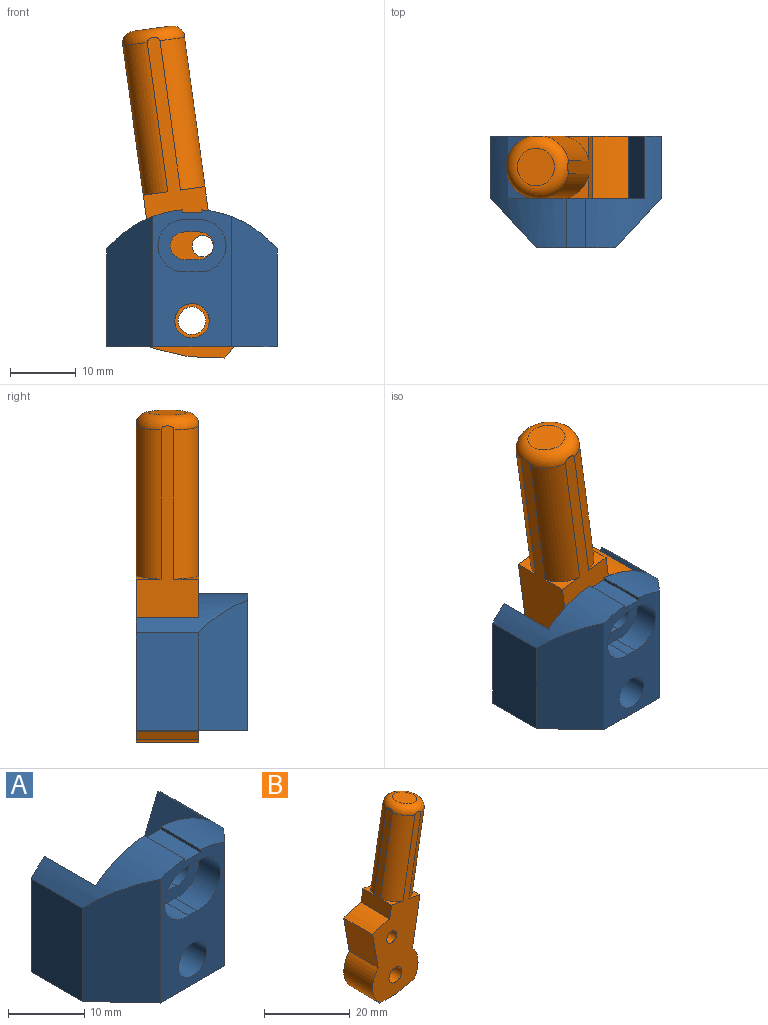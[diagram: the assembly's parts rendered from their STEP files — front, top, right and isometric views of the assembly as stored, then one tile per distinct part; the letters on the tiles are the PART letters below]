
ASSEMBLY  parts=2 mates=1
PART A: 28 faces, bbox 26x17x20.9 mm
  f0: plane 26x17mm, normal (0,0,-1), area 269mm2, adj f2,f8,f9,f10,f11,f12,f15,f16
  f1: cylinder r=17mm len=17mm, axis (0,1,0), area 98.1mm2, adj f2,f8,f11,f14,f16,f25,f27
  f2: plane 20.93x12mm, normal (0,-1,0), area 155.1mm2, adj f0,f1,f3,f17,f18,f19,f20,f21
  f3: cylinder r=17mm len=17mm, axis (0,1,0), area 98.1mm2, adj f2,f9,f10,f13,f16,f24,f26
  f4: cylinder r=9.4mm len=3.5mm, axis (0,-1,0), area 6.9mm2, adj f5,f7,f16,f22
  f5: cylinder r=2.1mm len=4.19mm, axis (0,-1,0), area 23.1mm2, adj f4,f6,f16,f22
  f6: cylinder r=13.6mm len=3.5mm, axis (0,-1,0), area 10mm2, adj f5,f7,f16,f22
  f7: cylinder r=2.1mm len=4.19mm, axis (0,-1,0), area 23.1mm2, adj f4,f6,f16,f22
  f8: plane 17.36x6.66mm, normal (0,1,0), area 85mm2, adj f0,f1,f11,f14,f15
  f9: plane 17.36x6.66mm, normal (0,1,0), area 85mm2, adj f0,f3,f10,f12,f13
  f10: plane 14.95x9.5mm, normal (1,0,0), area 142.1mm2, adj f0,f3,f9,f26
  f11: plane 14.95x9.5mm, normal (-1,0,0), area 142.1mm2, adj f0,f1,f8,f27
  f12: cylinder r=7.5mm len=9.5mm, axis (0,1,0), area 75.8mm2, adj f0,f9,f13,f16
  f13: plane 9.75x9.5mm, normal (-0.93,0,0.37), area 99.9mm2, adj f3,f9,f12,f16
  f14: plane 9.75x9.5mm, normal (0.93,0,0.37), area 99.9mm2, adj f1,f8,f15,f16
  f15: cylinder r=7.5mm len=9.5mm, axis (0,1,0), area 75.8mm2, adj f0,f8,f14,f16
  f16: plane 21.04x20.93mm, normal (0,1,0), area 280.9mm2, adj f0,f1,f3,f4,f5,f6,f7,f12
  f17: cylinder r=2.62mm len=7.5mm, axis (0,-1,0), area 123.7mm2, adj f2,f16
  f18: cylinder r=15.5mm len=4mm, axis (0,-1,0), area 13mm2, adj f2,f19,f21,f22
  f19: cylinder r=4mm len=7.98mm, axis (0,-1,0), area 50.3mm2, adj f2,f18,f20,f22
  f20: cylinder r=7.5mm len=4mm, axis (0,-1,0), area 6.3mm2, adj f2,f19,f21,f22
  f21: cylinder r=4mm len=7.98mm, axis (0,-1,0), area 50.3mm2, adj f2,f18,f20,f22
  f22: plane 10.4x8.06mm, normal (0,-1,0), area 45.6mm2, adj f4,f5,f6,f7,f18,f19,f20,f21
  f23: plane 7.5x3mm, normal (0,0,1), area 22.5mm2, adj f2,f16,f24,f25
  f24: plane 7.5x0.43mm, normal (-1,0,0), area 3.3mm2, adj f2,f3,f16,f23
  f25: plane 7.5x0.43mm, normal (1,0,0), area 3.3mm2, adj f1,f2,f16,f23
  f26: plane 19.91x7.5mm, normal (0.73,-0.68,0), area 183.4mm2, adj f0,f2,f3,f10
  f27: plane 19.91x7.5mm, normal (-0.73,-0.68,0), area 183.4mm2, adj f0,f1,f2,f11
PART B: 23 faces, bbox 20.1x10.5x50.4 mm
  f0: plane 3.77x3.71mm, normal (0.17,0,0.98), area 4.2mm2, adj f11,f15,f20
  f1: plane 3.77x3.71mm, normal (0.17,0,0.98), area 4.2mm2, adj f11,f16,f19
  f2: plane 3.77x3.71mm, normal (0.17,0,0.98), area 4.2mm2, adj f9,f16,f18
  f3: plane 10.36x9.5mm, normal (-0.98,0,-0.17), area 99.9mm2, adj f4,f12,f15,f16
  f4: cylinder r=7.5mm len=10.39mm, axis (0,1,0), area 109.3mm2, adj f3,f5,f15,f16
  f5: plane 9.5x5.1mm, normal (0,0,-1), area 48.4mm2, adj f4,f6,f15,f16
  f6: cylinder r=5.5mm len=9.5mm, axis (0,1,0), area 10.9mm2, adj f5,f7,f15,f16
  f7: plane 9.5x4.99mm, normal (0.21,0,-0.98), area 48.4mm2, adj f6,f8,f15,f16
  f8: cylinder r=7.5mm len=9.5mm, axis (0,1,0), area 94.3mm2, adj f7,f9,f15,f16
  f9: plane 37.25x9.5mm, normal (0.98,0,-0.17), area 180.9mm2, adj f2,f8,f10,f15,f16,f17,f18,f22
  f10: plane 3.77x3.71mm, normal (0.17,0,0.98), area 4.2mm2, adj f9,f15,f17
  f11: plane 26.89x9.5mm, normal (-0.98,0,0.17), area 81mm2, adj f0,f1,f12,f15,f16,f19,f20,f22
  f12: cylinder r=17mm len=9.5mm, axis (0,1,0), area 56.4mm2, adj f3,f11,f15,f16
  f13: cylinder r=1.62mm len=9.5mm, axis (0,1,0), area 97mm2, adj f15,f16
  f14: cylinder r=2.1mm len=9.5mm, axis (0,1,0), area 125.3mm2, adj f15,f16
  f15: plane 48.49x15.95mm, normal (0,-1,0), area 348.3mm2, adj f0,f3,f4,f5,f6,f7,f8,f9
  f16: plane 48.49x15.95mm, normal (0,1,0), area 348.3mm2, adj f1,f2,f3,f4,f5,f6,f7,f8
  f17: cylinder r=4.85mm len=23.31mm, axis (-0.17,0,-0.98), area 129.8mm2, adj f9,f10,f15,f22
  f18: cylinder r=4.85mm len=23.31mm, axis (-0.17,0,-0.98), area 129.8mm2, adj f2,f9,f16,f22
  f19: cylinder r=4.85mm len=23.31mm, axis (-0.17,0,-0.98), area 129.8mm2, adj f1,f11,f16,f22
  f20: cylinder r=4.85mm len=23.31mm, axis (-0.17,0,-0.98), area 129.8mm2, adj f0,f11,f15,f22
  f21: plane 5.7x5.61mm, normal (0.17,0,0.98), area 25.5mm2, adj f22
  f22: torus R=2.85mm, axis (0.17,0,0.98), area 77.5mm2, adj f9,f11,f15,f16,f17,f18,f19,f20
PLACE A t=(-7.72,3.72,-0.07)mm fixed
PLACE B rot(axis=(-0.02,0,-1),180deg) t=(-7.72,-1.03,-0.07)mm
MATE revolute B.f4 <-> A.f1  axis (0,-1,0) through (-7.72,-1.03,-0.07)mm
